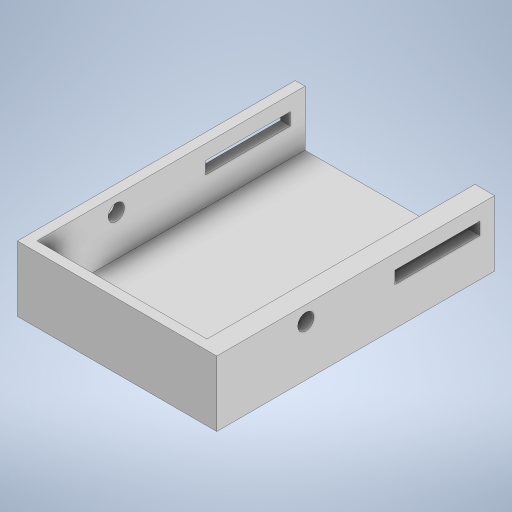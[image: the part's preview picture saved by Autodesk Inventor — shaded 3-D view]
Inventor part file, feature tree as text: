
AUTODESK INVENTOR PART (.ipt)
format: ipt  version: 2023 (Build 270158000, 158)  size: 269,312 bytes
history: native  units: in
note: dims shown in document units (in); Inventor stores cm internally (conversion verified against a paired STEP export)
features: sketch x6, extrude x5, shell x1
ambient origin geometry x8: Origin, YZ Plane, XZ Plane, XY Plane, X Axis, Y Axis, Z Axis, Center Point
bodies: Solid1 (feature_tree)
feature tree (12):
  extrude  "Extrusion1"  Depth=3.3465in
  shell  "Shell1"  Thickness=0.7874in
  sketch  "Sketch4"  dims[d4=0.1181in d17=0.3937in d18=0.0in]
  extrude  "Extrusion3"  Depth=0.3937in TaperAngle=0.0deg
  sketch  "Sketch6"  dims[d21=0.1772in d25=0.1181in d26=0.0in]
  extrude  "Extrusion5"  Depth=0.1496in
  extrude  "Extrusion6"  Depth=0.1181in TaperAngle=0.0deg
  extrude  "Extrusion7"  Depth=0.1969in
  sketch  "Sketch2"  dims[d0=2.2835in d1=3.3465in d2=0.7874in d3=0.0in]
  sketch  "Sketch5"  dims[d19=1.0236in d20=0.1496in]
  sketch  "Sketch7"  dims[d27=0.0in d28=0.0in d29=0.1969in]
  sketch  "Sketch8"  dims[d30=0.0in d31=0.0in d32=0.1772in d34=0.4606in d35=2.1457in d36=1.0728in d13=0.0197in d14=0.0344in d15=0.0197in d16=0.0344in d33=0.0344in]
